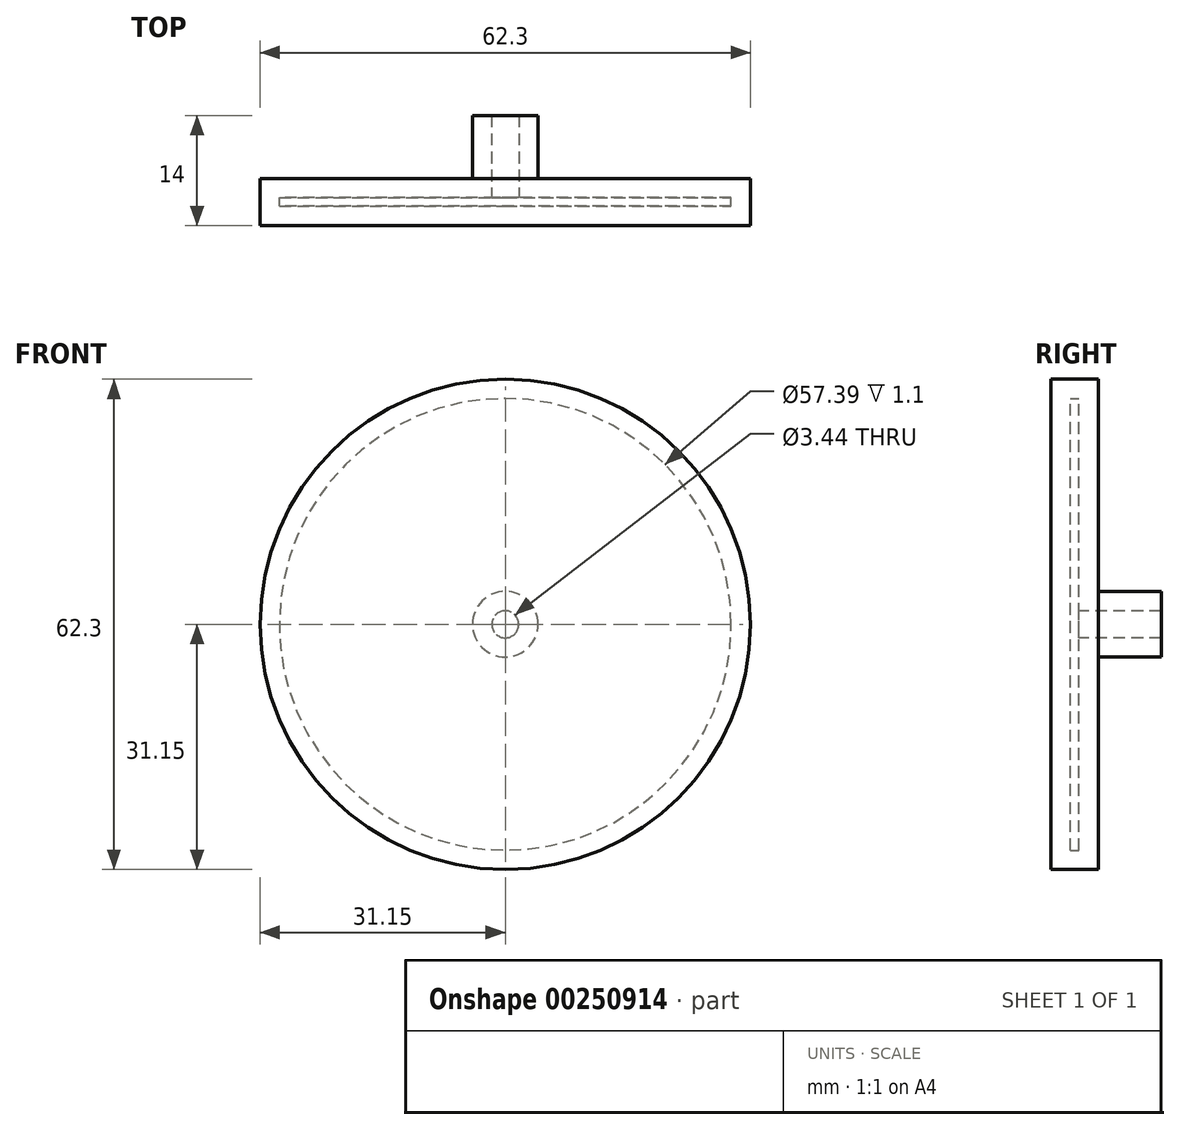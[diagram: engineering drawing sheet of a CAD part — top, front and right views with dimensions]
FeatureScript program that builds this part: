
annotation { "Feature Type Name" : "Feature", "Feature Type Description" : "" }
export const myFeature = defineFeature(function(context is Context, id is Id, definition is map)
    precondition{}
    {
        {
            var Q0;
            Q0=qCreatedBy(makeId("Front.planeOp"),FACE);
            var sketch = newSketch(context, id + "F0", { "sketchPlane" : qUnion([Q0])});
            skCircle(sketch, "E0", {"center": v(0, 0) * mm, "radius": 31.15 * mm});
            skSolve(sketch);
        }
        {
            var Q0;
            Q0=makeQuery(id+"F0.imprint","IMPRINT",FACE,{"disambiguationData":[TD([[makeQuery(id+"F0.imprint","IMPRINT",EDGE,{"derivedFrom":sQuery(id+"F0.wireOp",EDGE,"E0")}),1.0]])]});
            extrude(context, id + "F1", {"entities" : qUnion([Q0]), "depth" : 6 * mm});
        }
        {
            var Q0;
            Q0=makeQuery(id+"F1.opExtrude","CAP_FACE",FACE,{"disambiguationData":[OSD([sQuery(id+"F0.wireOp",EDGE,"E0")])],"isStart":true});
            var sketch = newSketch(context, id + "F2", { "sketchPlane" : qUnion([Q0])});
            skCircle(sketch, "E1", {"center": v(0, 0) * mm, "radius": 4.17 * mm});
            skSolve(sketch);
        }
        {
            var Q0;
            Q0=makeQuery(id+"F2.imprint","IMPRINT",FACE,{"disambiguationData":[TD([[makeQuery(id+"F2.imprint","IMPRINT",EDGE,{"derivedFrom":sQuery(id+"F2.wireOp",EDGE,"E1")}),1.0]])]});
            extrude(context, id + "F3", {"entities" : qUnion([Q0]), "operationType" : NewBodyOperationType.ADD, "depth" : 8 * mm});
        }
        {
            var Q0;
            Q0=makeQuery(id+"F3.opExtrude","CAP_FACE",FACE,{"disambiguationData":[OSD([sQuery(id+"F2.wireOp",EDGE,"E1")])],"isStart":false});
            shell(context, id + "F4", {"entities" : qUnion([Q0]), "thickness" : 2.45 * mm});
        }
    });
